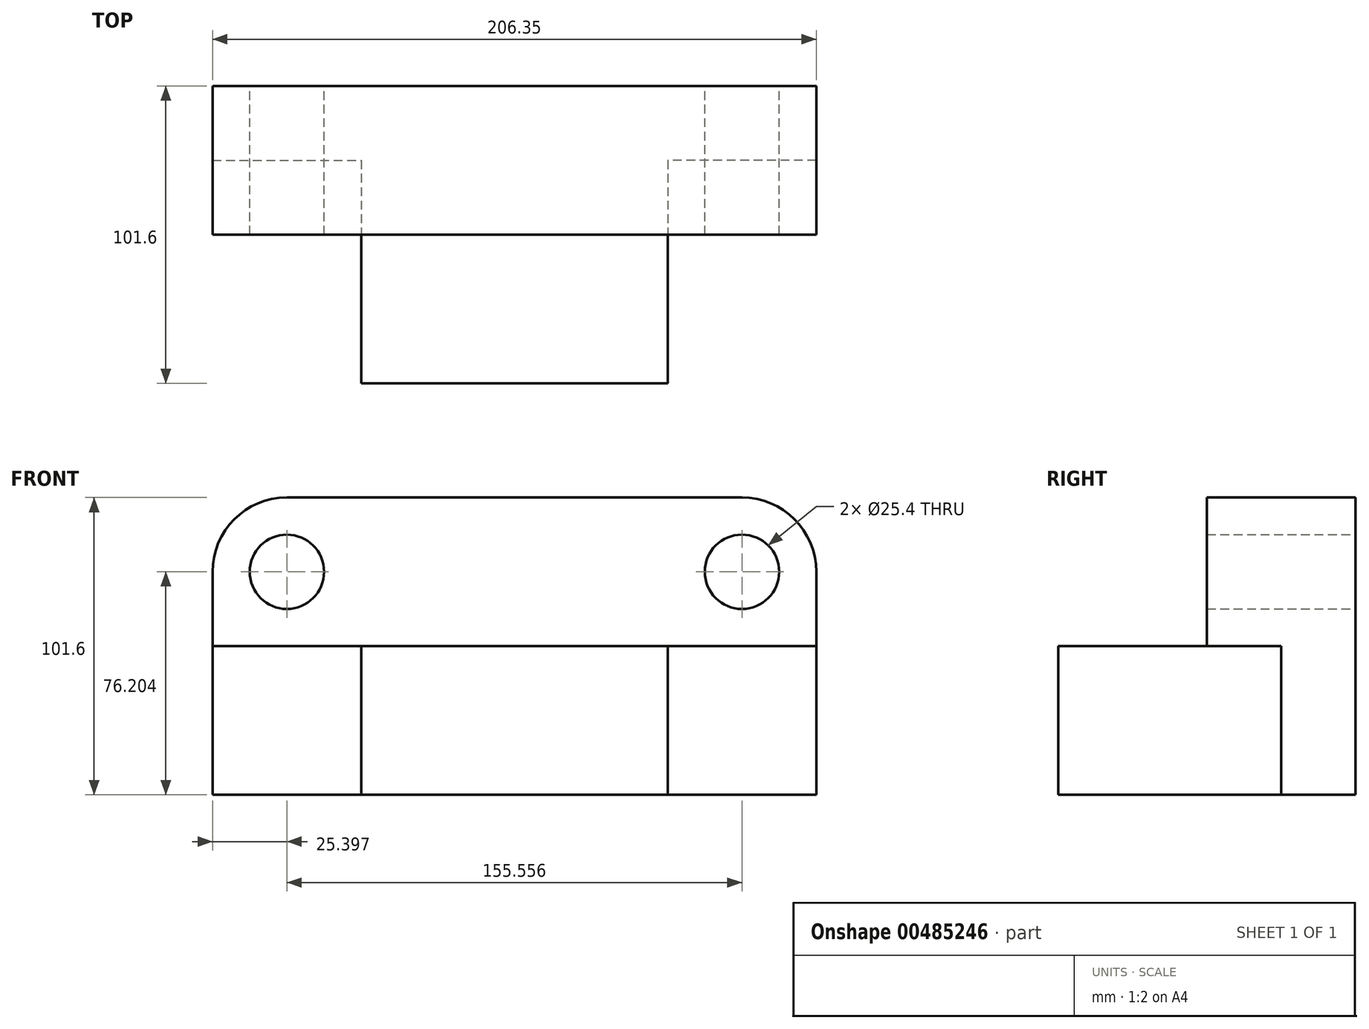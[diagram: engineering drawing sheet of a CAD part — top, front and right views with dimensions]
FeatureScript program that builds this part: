
annotation { "Feature Type Name" : "Feature", "Feature Type Description" : "" }
export const myFeature = defineFeature(function(context is Context, id is Id, definition is map)
    precondition{}
    {
        {
            var Q0;
            Q0=qCreatedBy(makeId("Front.planeOp"),FACE);
            var sketch = newSketch(context, id + "F0", { "sketchPlane" : qUnion([Q0])});
            skLineSegment(sketch, "E0.bottom", {"start": v(-69.51, 34.2) * mm, "end": v(86.04, 34.2) * mm});
            skLineSegment(sketch, "E0.top", {"start": v(-94.91, -67.4) * mm, "end": v(111.44, -67.4) * mm});
            skLineSegment(sketch, "E0.left", {"start": v(-94.91, 8.8) * mm, "end": v(-94.91, -67.4) * mm});
            skLineSegment(sketch, "E0.right", {"start": v(111.44, 8.8) * mm, "end": v(111.44, -67.4) * mm});
            skArc(sketch, "E1", {"start": v(-69.51, 34.2) * mm, "mid": v(-87.47, 26.75) * mm, "end": v(-94.91, 8.8) * mm});
            skArc(sketch, "E2", {"start": v(111.44, 8.8) * mm, "mid": v(104, 26.75) * mm, "end": v(86.04, 34.2) * mm});
            skPoint(sketch, "E3.orphan", {"position": v(111.44, 34.2) * mm});
            skCircle(sketch, "E4", {"center": v(86.04, 8.8) * mm, "radius": 12.7 * mm});
            skCircle(sketch, "E5", {"center": v(-69.51, 8.8) * mm, "radius": 12.7 * mm});
            skSolve(sketch);
        }
        {
            var Q0;
            Q0 = qSketchRegion(id + "F0", true);
            extrude(context, id + "F1", {"entities" : qUnion([Q0]), "depth" : 101.6 * mm});
        }
        {
            var Q0;
            Q0=makeQuery(id+"F1.opExtrude","CAP_FACE",FACE,{"disambiguationData":[OSD([sQuery(id+"F0.wireOp",EDGE,"E0.bottom"),sQuery(id+"F0.wireOp",EDGE,"E0.top"),sQuery(id+"F0.wireOp",EDGE,"E0.left"),sQuery(id+"F0.wireOp",EDGE,"E0.right")])],"isStart":false});
            var sketch = newSketch(context, id + "F2", { "sketchPlane" : qUnion([Q0])});
            skLineSegment(sketch, "E6.bottom", {"start": v(-94.91, -67.4) * mm, "end": v(-44.11, -67.4) * mm});
            skLineSegment(sketch, "E6.top", {"start": v(-94.91, -16.6) * mm, "end": v(-44.11, -16.6) * mm});
            skLineSegment(sketch, "E6.left", {"start": v(-94.91, -67.4) * mm, "end": v(-94.91, -16.6) * mm});
            skLineSegment(sketch, "E6.right", {"start": v(-44.11, -67.4) * mm, "end": v(-44.11, -16.6) * mm});
            skLineSegment(sketch, "E7.bottom", {"start": v(111.44, -67.4) * mm, "end": v(60.64, -67.4) * mm});
            skLineSegment(sketch, "E7.top", {"start": v(111.44, -16.6) * mm, "end": v(60.64, -16.6) * mm});
            skLineSegment(sketch, "E7.left", {"start": v(111.44, -67.4) * mm, "end": v(111.44, -16.6) * mm});
            skLineSegment(sketch, "E7.right", {"start": v(60.64, -67.4) * mm, "end": v(60.64, -16.6) * mm});
            skSolve(sketch);
        }
        {
            var Q0;
            Q0 = qSketchRegion(id + "F2", true);
            extrude(context, id + "F3", {"entities" : qUnion([Q0]), "operationType" : NewBodyOperationType.REMOVE, "oppositeDirection" : true, "depth" : 76.2 * mm});
        }
        {
            var Q0;
            Q0=makeQuery(id+"F1.opExtrude","CAP_FACE",FACE,{"disambiguationData":[OSD([sQuery(id+"F0.wireOp",EDGE,"E0.bottom"),sQuery(id+"F0.wireOp",EDGE,"E0.top"),sQuery(id+"F0.wireOp",EDGE,"E0.left"),sQuery(id+"F0.wireOp",EDGE,"E0.right")])],"isStart":false});
            var sketch = newSketch(context, id + "F4", { "sketchPlane" : qUnion([Q0])});
            skLineSegment(sketch, "E8.bottom", {"start": v(-69.51, 34.2) * mm, "end": v(111.44, 34.2) * mm});
            skLineSegment(sketch, "E8.top", {"start": v(-69.51, -16.6) * mm, "end": v(111.44, -16.6) * mm});
            skLineSegment(sketch, "E8.left", {"start": v(-69.51, 34.2) * mm, "end": v(-69.51, -16.6) * mm});
            skLineSegment(sketch, "E8.right", {"start": v(111.44, 34.2) * mm, "end": v(111.44, -16.6) * mm});
            skSolve(sketch);
        }
        {
            var Q0;
            Q0 = qSketchRegion(id + "F4", true);
            extrude(context, id + "F5", {"entities" : qUnion([Q0]), "operationType" : NewBodyOperationType.REMOVE, "oppositeDirection" : true, "depth" : 50.8 * mm});
        }
        {
            var Q0;
            Q0=makeQuery(id+"F5.boolean.opBoolean","COPY",FACE,{"derivedFrom":makeQuery(id+"F5.opExtrude","SWEPT_FACE",FACE,{"disambiguationData":[OSD([sQuery(id+"F4.wireOp",EDGE,"E8.left")])]})});
            var sketch = newSketch(context, id + "F6", { "sketchPlane" : qUnion([Q0])});
            skLineSegment(sketch, "E9.bottom", {"start": v(-101.6, 34.2) * mm, "end": v(-50.8, 34.2) * mm});
            skLineSegment(sketch, "E9.top", {"start": v(-101.6, -16.6) * mm, "end": v(-50.8, -16.6) * mm});
            skLineSegment(sketch, "E9.left", {"start": v(-101.6, 34.2) * mm, "end": v(-101.6, -16.6) * mm});
            skLineSegment(sketch, "E9.right", {"start": v(-50.8, 34.2) * mm, "end": v(-50.8, -16.6) * mm});
            skSolve(sketch);
        }
        {
            var Q0;
            Q0 = qSketchRegion(id + "F6", true);
            extrude(context, id + "F7", {"entities" : qUnion([Q0]), "operationType" : NewBodyOperationType.REMOVE, "oppositeDirection" : true, "depth" : 203.2 * mm});
        }
    });
